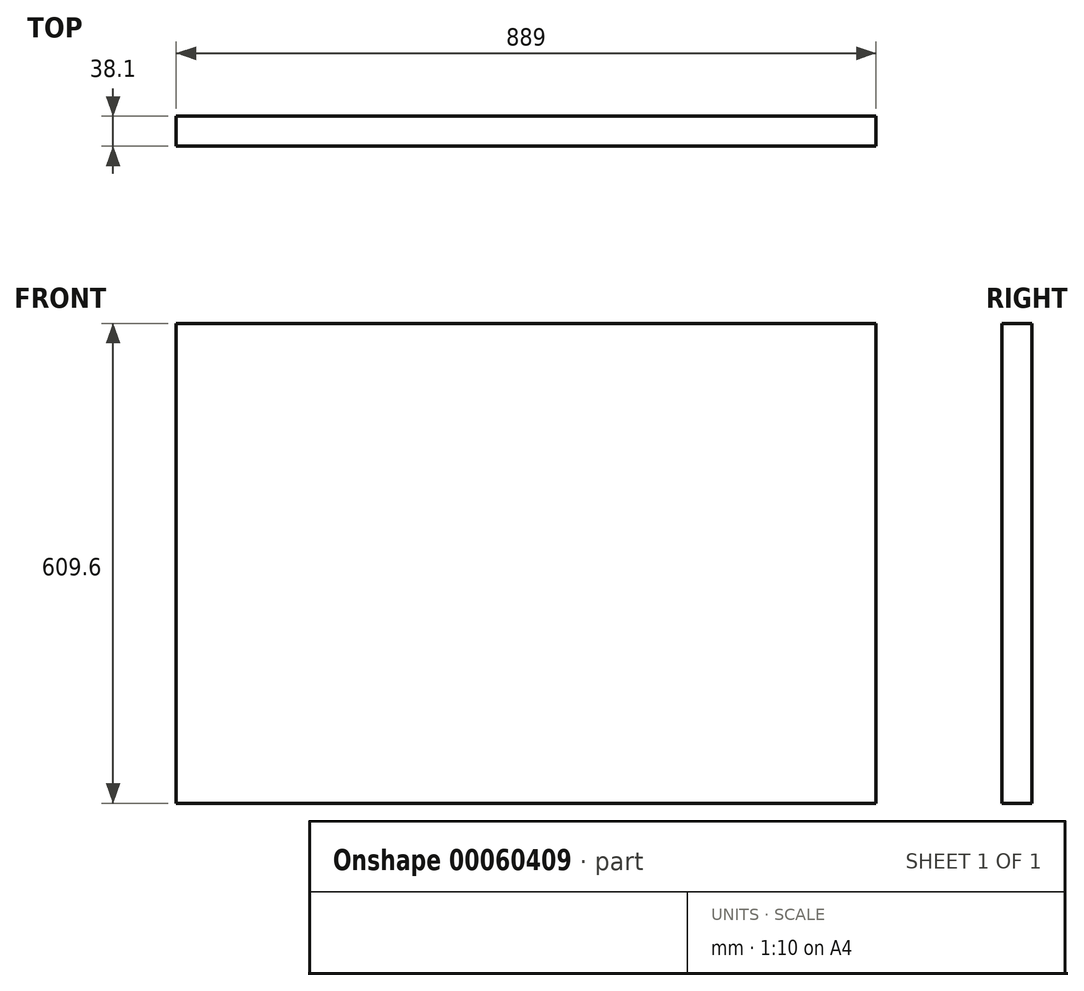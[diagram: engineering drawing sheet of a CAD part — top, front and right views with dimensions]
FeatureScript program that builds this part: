
annotation { "Feature Type Name" : "Feature", "Feature Type Description" : "" }
export const myFeature = defineFeature(function(context is Context, id is Id, definition is map)
    precondition{}
    {
        {
            var Q0;
            Q0=qCreatedBy(makeId("Right.planeOp"),FACE);
            var sketch = newSketch(context, id + "F0", { "sketchPlane" : qUnion([Q0])});
            skLineSegment(sketch, "E0.bottom", {"start": v(0, 0) * mm, "end": v(-38.1, 0) * mm});
            skLineSegment(sketch, "E0.top", {"start": v(0, 609.6) * mm, "end": v(-38.1, 609.6) * mm});
            skLineSegment(sketch, "E0.left", {"start": v(0, 0) * mm, "end": v(0, 609.6) * mm});
            skLineSegment(sketch, "E0.right", {"start": v(-38.1, 0) * mm, "end": v(-38.1, 609.6) * mm});
            skSolve(sketch);
        }
        {
            var Q0;
            Q0=makeQuery(id+"F0.imprint","IMPRINT",FACE,{"disambiguationData":[TD([[makeQuery(id+"F0.imprint","IMPRINT",EDGE,{"derivedFrom":sQuery(id+"F0.wireOp",EDGE,"E0.bottom")}),-1.0]])]});
            extrude(context, id + "F1", {"entities" : qUnion([Q0]), "depth" : 889 * mm});
        }
    });
